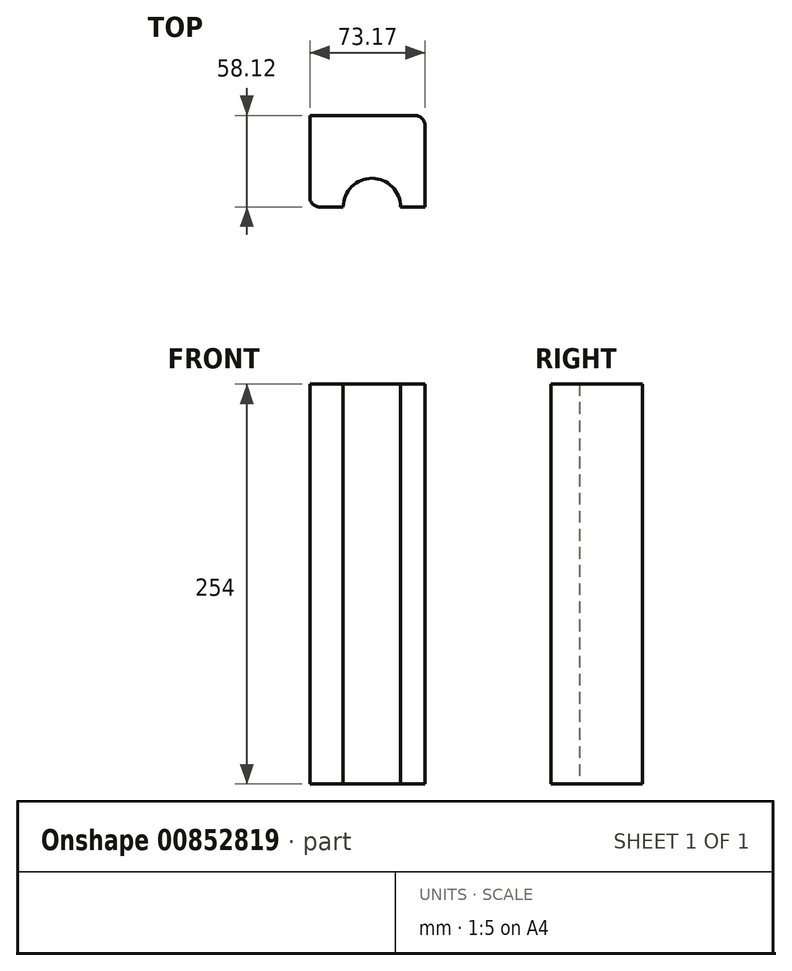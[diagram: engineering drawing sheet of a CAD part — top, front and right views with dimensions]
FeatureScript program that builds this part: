
annotation { "Feature Type Name" : "Feature", "Feature Type Description" : "" }
export const myFeature = defineFeature(function(context is Context, id is Id, definition is map)
    precondition{}
    {
        {
            var Q0;
            Q0=qCreatedBy(makeId("Top.planeOp"),FACE);
            var sketch = newSketch(context, id + "F0", { "sketchPlane" : qUnion([Q0])});
            skLineSegment(sketch, "E0.bottom", {"start": v(-26.66, -28.76) * mm, "end": v(-11.74, -28.76) * mm});
            skLineSegment(sketch, "E0.top", {"start": v(-33, 29.36) * mm, "end": v(33.81, 29.36) * mm});
            skLineSegment(sketch, "E0.left", {"start": v(-33, -22.41) * mm, "end": v(-33, 29.36) * mm});
            skLineSegment(sketch, "E0.right", {"start": v(40.16, -28.76) * mm, "end": v(40.16, 23.01) * mm});
            skArc(sketch, "E1", {"start": v(24.71, -28.76) * mm, "mid": v(6.48, -10.53) * mm, "end": v(-11.74, -28.76) * mm});
            skLineSegment(sketch, "E2.trimOffspring", {"start": v(24.71, -28.76) * mm, "end": v(40.16, -28.76) * mm});
            skPoint(sketch, "E3.visualSharp", {"position": v(40.16, 29.36) * mm});
            skArc(sketch, "E3.filletArc", {"start": v(40.16, 23.01) * mm, "mid": v(38.3, 27.5) * mm, "end": v(33.81, 29.36) * mm});
            skPoint(sketch, "E4.visualSharp", {"position": v(-33, -28.76) * mm});
            skArc(sketch, "E4.filletArc", {"start": v(-33, -22.41) * mm, "mid": v(-31.15, -26.9) * mm, "end": v(-26.66, -28.76) * mm});
            skSolve(sketch);
        }
        {
            var Q0;
            Q0=makeQuery(id+"F0.imprint","IMPRINT",FACE,{"disambiguationData":[TD([[makeQuery(id+"F0.imprint","IMPRINT",EDGE,{"derivedFrom":sQuery(id+"F0.wireOp",EDGE,"E0.bottom")}),1.0]])]});
            extrude(context, id + "F1", {"entities" : qUnion([Q0]), "endBound" : BoundingType.SYMMETRIC, "depth" : 254 * mm, "offsetDistance" : 25.4 * mm});
        }
    });
